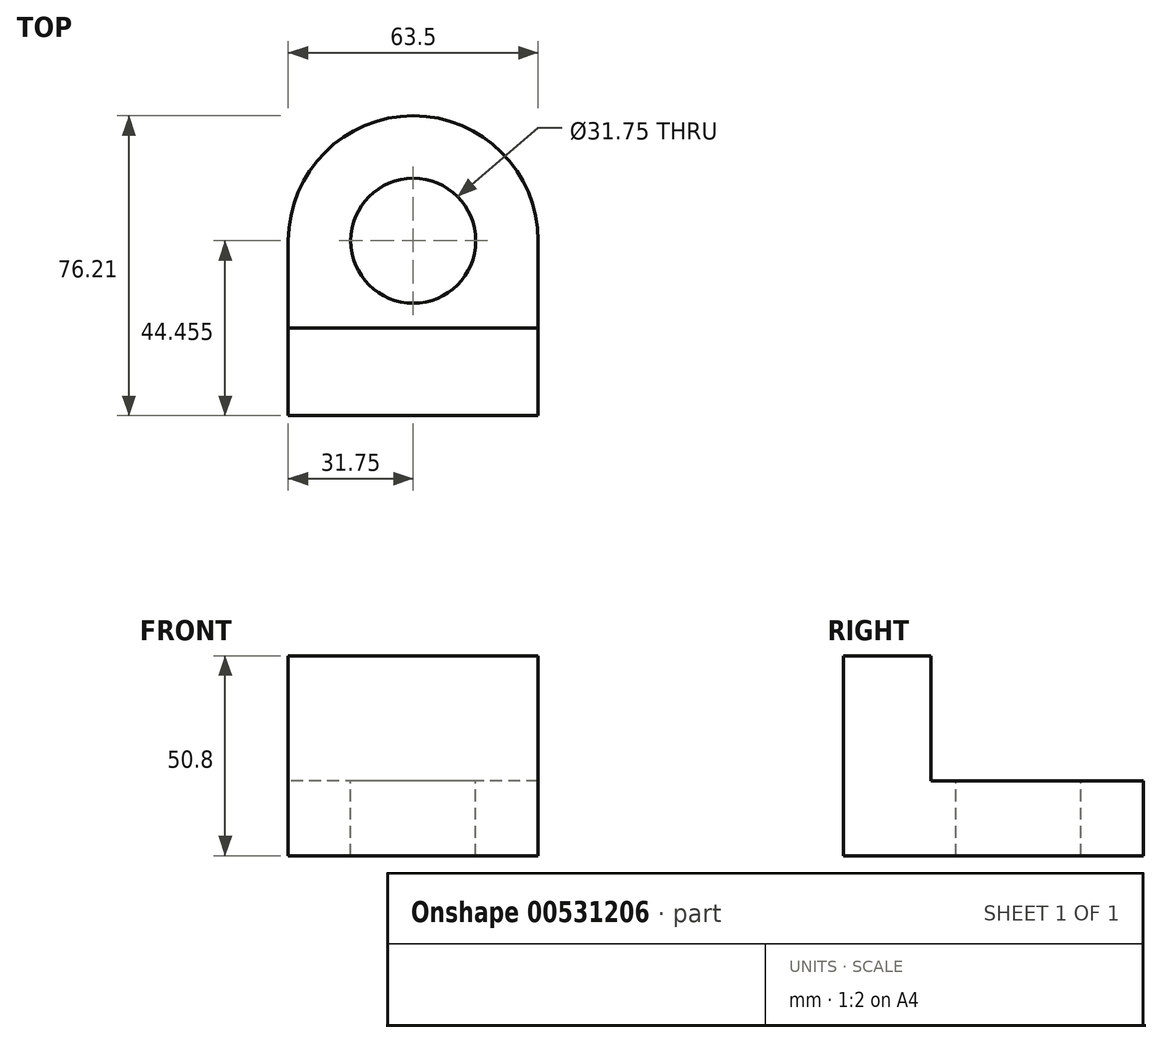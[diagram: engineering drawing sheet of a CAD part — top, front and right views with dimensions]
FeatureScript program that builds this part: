
annotation { "Feature Type Name" : "Feature", "Feature Type Description" : "" }
export const myFeature = defineFeature(function(context is Context, id is Id, definition is map)
    precondition{}
    {
        {
            var Q0;
            Q0=qCreatedBy(makeId("Top.planeOp"),FACE);
            var sketch = newSketch(context, id + "F0", { "sketchPlane" : qUnion([Q0])});
            skLineSegment(sketch, "E0.bottom", {"start": v(31.75, -22.23) * mm, "end": v(-31.75, -22.23) * mm});
            skLineSegment(sketch, "E0.top", {"start": v(31.75, 22.22) * mm, "end": v(-31.75, 22.22) * mm});
            skLineSegment(sketch, "E0.left", {"start": v(31.75, -22.23) * mm, "end": v(31.75, 22.22) * mm});
            skLineSegment(sketch, "E0.right", {"start": v(-31.75, -22.23) * mm, "end": v(-31.75, 22.22) * mm});
            skPoint(sketch, "E0.middle", {"position": v(0, 0) * mm});
            skArc(sketch, "E1", {"start": v(-31.75, 22.23) * mm, "mid": v(0, 53.98) * mm, "end": v(31.75, 22.22) * mm});
            skSolve(sketch);
        }
        {
            var Q0;
            Q0 = qSketchRegion(id + "F0", true);
            extrude(context, id + "F1", {"entities" : qUnion([Q0]), "depth" : 19.05 * mm, "offsetDistance" : 25.4 * mm});
        }
        {
            var Q0;
            Q0=makeQuery(id+"F1.opExtrude","CAP_FACE",FACE,{"disambiguationData":[OSD([sQuery(id+"F0.wireOp",EDGE,"E0.bottom"),sQuery(id+"F0.wireOp",EDGE,"E0.left"),sQuery(id+"F0.wireOp",EDGE,"E0.right"),sQuery(id+"F0.wireOp",EDGE,"E1")])],"isStart":false});
            var sketch = newSketch(context, id + "F2", { "sketchPlane" : qUnion([Q0])});
            skCircle(sketch, "E2", {"center": v(0, 22.23) * mm, "radius": 15.88 * mm});
            skSolve(sketch);
        }
        {
            var Q0;
            Q0=makeQuery(id+"F2.imprint","IMPRINT",FACE,{"disambiguationData":[TD([[makeQuery(id+"F2.imprint","IMPRINT",EDGE,{"derivedFrom":sQuery(id+"F2.wireOp",EDGE,"E2")}),1.0]])]});
            extrude(context, id + "F3", {"entities" : qUnion([Q0]), "operationType" : NewBodyOperationType.REMOVE, "oppositeDirection" : true, "depth" : 25.4 * mm, "offsetDistance" : 25.4 * mm});
        }
        {
            var Q0;
            Q0=qCreatedBy(makeId("Top.planeOp"),FACE);
            var sketch = newSketch(context, id + "F4", { "sketchPlane" : qUnion([Q0])});
            skLineSegment(sketch, "E3.bottom", {"start": v(-31.75, -22.23) * mm, "end": v(31.75, -22.23) * mm});
            skLineSegment(sketch, "E3.top", {"start": v(-31.75, 0) * mm, "end": v(31.75, 0) * mm});
            skLineSegment(sketch, "E3.left", {"start": v(-31.75, -22.23) * mm, "end": v(-31.75, 0) * mm});
            skLineSegment(sketch, "E3.right", {"start": v(31.75, -22.23) * mm, "end": v(31.75, 0) * mm});
            skSolve(sketch);
        }
        {
            var Q0;
            Q0 = qSketchRegion(id + "F4", true);
            extrude(context, id + "F5", {"entities" : qUnion([Q0]), "operationType" : NewBodyOperationType.ADD, "depth" : 50.8 * mm, "offsetDistance" : 25.4 * mm});
        }
    });
